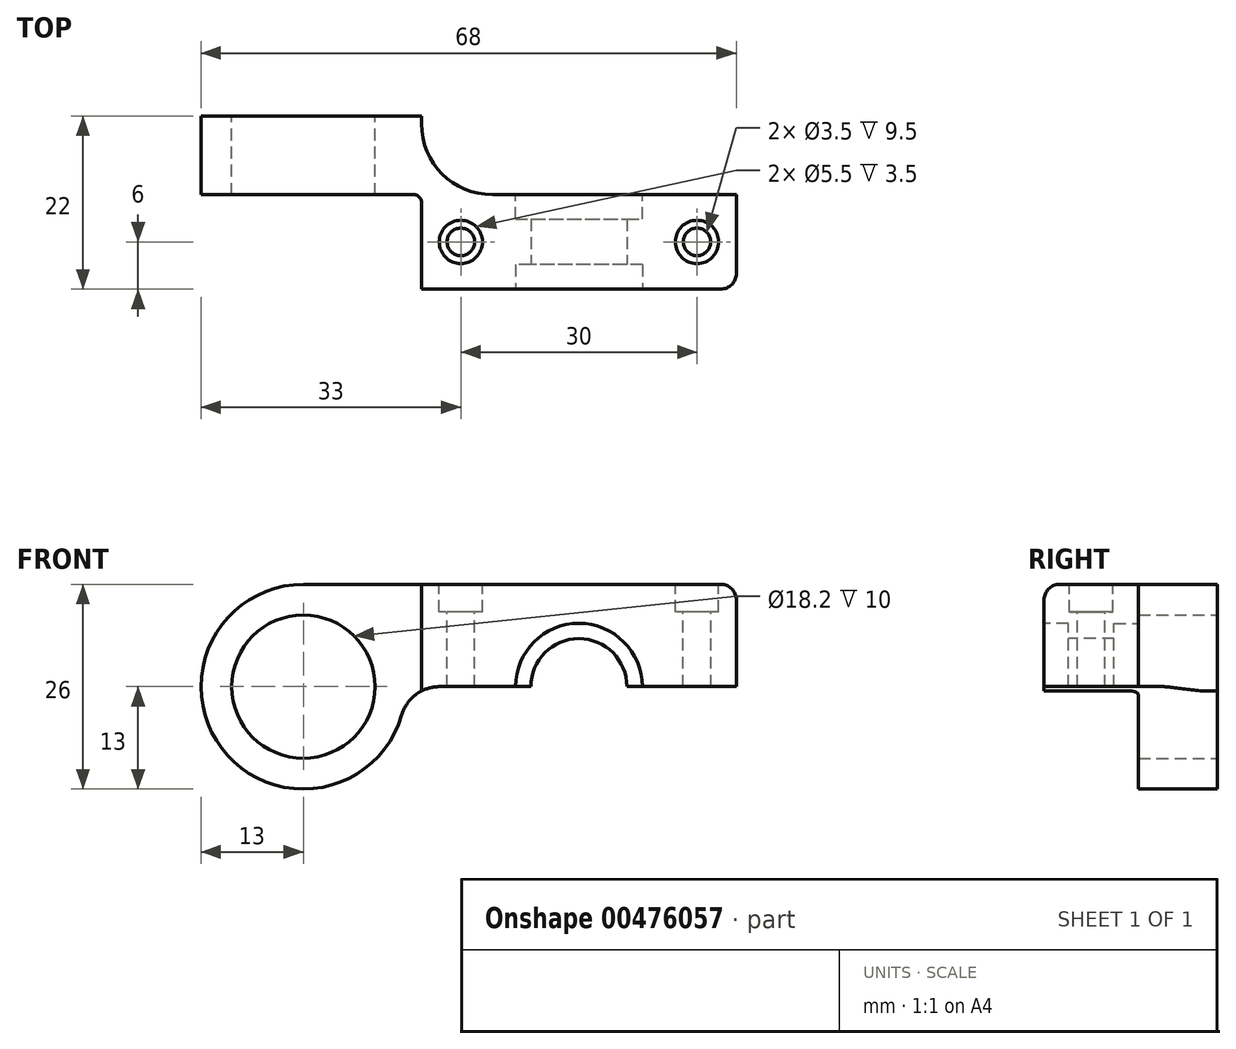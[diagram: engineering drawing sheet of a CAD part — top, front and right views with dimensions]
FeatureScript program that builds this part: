
annotation { "Feature Type Name" : "Feature", "Feature Type Description" : "" }
export const myFeature = defineFeature(function(context is Context, id is Id, definition is map)
    precondition{}
    {
        {
            var Q0;
            Q0=qCreatedBy(makeId("Front.planeOp"),FACE);
            var sketch = newSketch(context, id + "F0", { "sketchPlane" : qUnion([Q0])});
            skCircle(sketch, "E0", {"center": v(-35, 0) * mm, "radius": 9.1 * mm});
            skCircle(sketch, "E1", {"center": v(0, 0) * mm, "radius": 15 * mm, "construction": true});
            skArc(sketch, "E2", {"start": v(-35, 13) * mm, "mid": v(-44.2, -9.2) * mm, "end": v(-22, 0) * mm});
            skLineSegment(sketch, "E3", {"start": v(-35, 13) * mm, "end": v(20, 13) * mm});
            skLineSegment(sketch, "E4", {"start": v(20, 13) * mm, "end": v(20, 0) * mm});
            skLineSegment(sketch, "E5", {"start": v(20, 0) * mm, "end": v(-22, 0) * mm});
            skSolve(sketch);
        }
        {
            var Q0;
            Q0 = qSketchRegion(id + "F0", true);
            extrude(context, id + "F1", {"entities" : qUnion([Q0]), "depth" : 22 * mm});
        }
        {
            var Q0;
            Q0=makeQuery(id+"F1.opExtrude","CAP_FACE",FACE,{"disambiguationData":[OSD([sQuery(id+"F0.wireOp",EDGE,"E0"),sQuery(id+"F0.wireOp",EDGE,"E2"),sQuery(id+"F0.wireOp",EDGE,"E3"),sQuery(id+"F0.wireOp",EDGE,"E4"),sQuery(id+"F0.wireOp",EDGE,"E5")])],"isStart":false});
            var sketch = newSketch(context, id + "F2", { "sketchPlane" : qUnion([Q0])});
            skCircle(sketch, "E6", {"center": v(-35, 0) * mm, "radius": 13 * mm});
            skSolve(sketch);
        }
        {
            var Q0;
            Q0 = qSketchRegion(id + "F2", true);
            extrude(context, id + "F3", {"entities" : qUnion([Q0]), "operationType" : NewBodyOperationType.REMOVE, "oppositeDirection" : true, "depth" : 12 * mm});
        }
        {
            var Q0;
            Q0=makeQuery(id+"F1.opExtrude","SWEPT_FACE",FACE,{"disambiguationData":[OSD([sQuery(id+"F0.wireOp",EDGE,"E3")])]});
            var sketch = newSketch(context, id + "F4", { "sketchPlane" : qUnion([Q0])});
            skCircle(sketch, "E7", {"center": v(-15, -16) * mm, "radius": 1.75 * mm});
            skCircle(sketch, "E8.MirrorC", {"center": v(15, -16) * mm, "radius": 1.75 * mm});
            skSolve(sketch);
        }
        {
            var Q0;
            Q0 = qSketchRegion(id + "F4", true);
            extrude(context, id + "F5", {"entities" : qUnion([Q0]), "operationType" : NewBodyOperationType.REMOVE, "endBound" : BoundingType.THROUGH_ALL, "oppositeDirection" : true, "depth" : 25 * mm});
        }
        {
            var Q0;
            Q0=makeQuery(id+"F1.opExtrude","SWEPT_FACE",FACE,{"disambiguationData":[OSD([sQuery(id+"F0.wireOp",EDGE,"E3")])]});
            var sketch = newSketch(context, id + "F6", { "sketchPlane" : qUnion([Q0])});
            skLineSegment(sketch, "E9.left", {"start": v(20, 0) * mm, "end": v(20, -10) * mm});
            skLineSegment(sketch, "E10.MirrorCS", {"start": v(-20, 0) * mm, "end": v(-20, -1) * mm});
            skLineSegment(sketch, "E11", {"start": v(20, -10) * mm, "end": v(-11, -10) * mm});
            skLineSegment(sketch, "E12", {"start": v(-20, 0) * mm, "end": v(20, 0) * mm});
            skPoint(sketch, "E13.visualSharp", {"position": v(-20, -10) * mm});
            skArc(sketch, "E13.filletArc", {"start": v(-20, -1) * mm, "mid": v(-17.36, -7.36) * mm, "end": v(-11, -10) * mm});
            skSolve(sketch);
        }
        {
            var Q0;
            Q0 = qSketchRegion(id + "F6", true);
            extrude(context, id + "F7", {"entities" : qUnion([Q0]), "operationType" : NewBodyOperationType.REMOVE, "oppositeDirection" : true, "depth" : 25 * mm});
        }
        {
            var Q0;
            Q0=makeQuery(id+"F1.opExtrude","SWEPT_FACE",FACE,{"disambiguationData":[OSD([sQuery(id+"F0.wireOp",EDGE,"E3")])]});
            var sketch = newSketch(context, id + "F8", { "sketchPlane" : qUnion([Q0])});
            skLineSegment(sketch, "E14.bottom", {"start": v(-35, -22) * mm, "end": v(-20, -22) * mm});
            skLineSegment(sketch, "E14.top", {"start": v(-35, -10) * mm, "end": v(-20, -10) * mm});
            skLineSegment(sketch, "E14.left", {"start": v(-35, -22) * mm, "end": v(-35, -10) * mm});
            skLineSegment(sketch, "E14.right", {"start": v(-20, -22) * mm, "end": v(-20, -10) * mm});
            skSolve(sketch);
        }
        {
            var Q0;
            Q0 = qSketchRegion(id + "F8", true);
            extrude(context, id + "F9", {"entities" : qUnion([Q0]), "operationType" : NewBodyOperationType.REMOVE, "oppositeDirection" : true, "depth" : 25 * mm});
        }
        {
            var Q0;
            Q0=makeQuery(id+"F1.opExtrude","CAP_FACE",FACE,{"disambiguationData":[OSD([sQuery(id+"F0.wireOp",EDGE,"E0"),sQuery(id+"F0.wireOp",EDGE,"E2"),sQuery(id+"F0.wireOp",EDGE,"E3"),sQuery(id+"F0.wireOp",EDGE,"E4"),sQuery(id+"F0.wireOp",EDGE,"E5")])],"isStart":false});
            var sketch = newSketch(context, id + "F10", { "sketchPlane" : qUnion([Q0])});
            skCircle(sketch, "E15", {"center": v(0, 0) * mm, "radius": 6.1 * mm});
            skSolve(sketch);
        }
        {
            var Q0;
            Q0 = qSketchRegion(id + "F10", true);
            extrude(context, id + "F11", {"entities" : qUnion([Q0]), "operationType" : NewBodyOperationType.REMOVE, "oppositeDirection" : true, "depth" : 25 * mm});
        }
        {
            var Q0;
            Q0=makeQuery(id+"F7.boolean.opBoolean","COPY",FACE,{"derivedFrom":makeQuery(id+"F7.opExtrude","SWEPT_FACE",FACE,{"disambiguationData":[OSD([sQuery(id+"F6.wireOp",EDGE,"E11")])]})});
            var sketch = newSketch(context, id + "F12", { "sketchPlane" : qUnion([Q0])});
            skCircle(sketch, "E16", {"center": v(0, 0) * mm, "radius": 8.05 * mm});
            skSolve(sketch);
        }
        {
            var Q0;
            Q0 = qSketchRegion(id + "F12", true);
            extrude(context, id + "F13", {"entities" : qUnion([Q0]), "operationType" : NewBodyOperationType.REMOVE, "oppositeDirection" : true, "depth" : 3.1 * mm});
        }
        {
            var Q0;
            Q0=makeQuery(id+"F1.opExtrude","CAP_FACE",FACE,{"disambiguationData":[OSD([sQuery(id+"F0.wireOp",EDGE,"E0"),sQuery(id+"F0.wireOp",EDGE,"E2"),sQuery(id+"F0.wireOp",EDGE,"E3"),sQuery(id+"F0.wireOp",EDGE,"E4"),sQuery(id+"F0.wireOp",EDGE,"E5")])],"isStart":false});
            var sketch = newSketch(context, id + "F14", { "sketchPlane" : qUnion([Q0])});
            skCircle(sketch, "E17", {"center": v(0, 0) * mm, "radius": 8.05 * mm});
            skSolve(sketch);
        }
        {
            var Q0;
            Q0 = qSketchRegion(id + "F14", true);
            extrude(context, id + "F15", {"entities" : qUnion([Q0]), "operationType" : NewBodyOperationType.REMOVE, "oppositeDirection" : true, "depth" : 3.1 * mm});
        }
        {
            var Q0;
            Q0=makeQuery(id+"F9.boolean.opBoolean","COPY",EDGE,{"derivedFrom":makeQuery(id+"F9.opExtrude","SWEPT_EDGE",EDGE,{"disambiguationData":[OSD([sQuery(id+"F8.wireOp",EDGE,"E14.top"),sQuery(id+"F8.wireOp",EDGE,"E14.right")])]})});
            fillet(context, id + "F16", {"entities" : qUnion([Q0]), "radius" : 1 * mm, "tangentPropagation" : true, "allowEdgeOverflow" : false});
        }
        {
            var Q0;
            Q0=makeQuery(id+"F7.boolean.opBoolean","COPY",EDGE,{"derivedFrom":makeQuery(id+"F7.opExtrude","CAP_EDGE",EDGE,{"disambiguationData":[OSD([sQuery(id+"F6.wireOp",EDGE,"E11")])],"isStart":true})});
            var Q1;
            Q1=makeQuery(id+"F1.opExtrude","SWEPT_EDGE",EDGE,{"disambiguationData":[OSD([sQuery(id+"F0.wireOp",EDGE,"E3"),sQuery(id+"F0.wireOp",EDGE,"E4")])]});
            var Q2;
            Q2=makeQuery(id+"F1.opExtrude","CAP_EDGE",EDGE,{"disambiguationData":[OSD([sQuery(id+"F0.wireOp",EDGE,"E3")])],"isStart":false});
            var Q3;
            Q3=makeQuery(id+"F9.boolean.opBoolean","COPY",EDGE,{"derivedFrom":makeQuery(id+"F9.opExtrude","CAP_EDGE",EDGE,{"disambiguationData":[OSD([sQuery(id+"F8.wireOp",EDGE,"E14.right")])],"isStart":true})});
            var Q4;
            Q4=makeQuery(id+"F9.boolean.opBoolean","COPY",EDGE,{"derivedFrom":makeQuery(id+"F9.opExtrude","SWEPT_EDGE",EDGE,{"disambiguationData":[OSD([sQuery(id+"F0.wireOp",EDGE,"E3"),sQuery(id+"F8.wireOp",EDGE,"E14.bottom"),sQuery(id+"F8.wireOp",EDGE,"E14.right")])]})});
            var Q5;
            Q5=makeQuery(id+"F1.opExtrude","CAP_EDGE",EDGE,{"disambiguationData":[OSD([sQuery(id+"F0.wireOp",EDGE,"E4")])],"isStart":false});
            var Q6;
            Q6=makeQuery(id+"F7.boolean.opBoolean","COPY",EDGE,{"derivedFrom":makeQuery(id+"F7.opExtrude","SWEPT_EDGE",EDGE,{"disambiguationData":[OSD([sQuery(id+"F0.wireOp",EDGE,"E3"),sQuery(id+"F0.wireOp",EDGE,"E4"),sQuery(id+"F6.wireOp",EDGE,"E9.left"),sQuery(id+"F6.wireOp",EDGE,"E11")])]})});
            var Q7;
            Q7=makeQuery(id+"F7.boolean.opBoolean","COPY",EDGE,{"derivedFrom":makeQuery(id+"F7.opExtrude","SWEPT_EDGE",EDGE,{"disambiguationData":[OSD([sQuery(id+"F0.wireOp",EDGE,"E3"),sQuery(id+"F6.wireOp",EDGE,"E10.MirrorCS"),sQuery(id+"F6.wireOp",EDGE,"E12")])]})});
            fillet(context, id + "F17", {"entities" : qUnion([Q0, Q1, Q2, Q3, Q4, Q5, Q6, Q7]), "radius" : 2 * mm, "tangentPropagation" : true, "allowEdgeOverflow" : false});
        }
        {
            var Q0;
            {var subQ0=sQuery(id+"F0.wireOp",EDGE,"E2");var subQ1=sQuery(id+"F0.wireOp",EDGE,"E5");Q0=makeQuery(id+"F3.boolean.opBoolean","SPLIT",EDGE,{"disambiguationData":[topologyDisambiguationEdgeConnected([makeQuery(id+"F1.opExtrude","SWEPT_FACE",FACE,{"disambiguationData":[OSD([subQ0])]})])],"derivedFrom":makeQuery(id+"F1.opExtrude","SWEPT_EDGE",EDGE,{"disambiguationData":[OSD([subQ0,subQ1])]})});}
            fillet(context, id + "F18", {"entities" : qUnion([Q0]), "radius" : 5 * mm, "tangentPropagation" : true, "allowEdgeOverflow" : false});
        }
        {
            var Q0;
            Q0=makeQuery(id+"F1.opExtrude","SWEPT_FACE",FACE,{"disambiguationData":[OSD([sQuery(id+"F0.wireOp",EDGE,"E3")])]});
            var sketch = newSketch(context, id + "F19", { "sketchPlane" : qUnion([Q0])});
            skCircle(sketch, "E18", {"center": v(15, -16) * mm, "radius": 2.75 * mm});
            skCircle(sketch, "E19.MirrorC", {"center": v(-15, -16) * mm, "radius": 2.75 * mm});
            skSolve(sketch);
        }
        {
            var Q0;
            Q0 = qSketchRegion(id + "F19", true);
            extrude(context, id + "F20", {"entities" : qUnion([Q0]), "operationType" : NewBodyOperationType.REMOVE, "oppositeDirection" : true, "depth" : 3.5 * mm});
        }
    });
